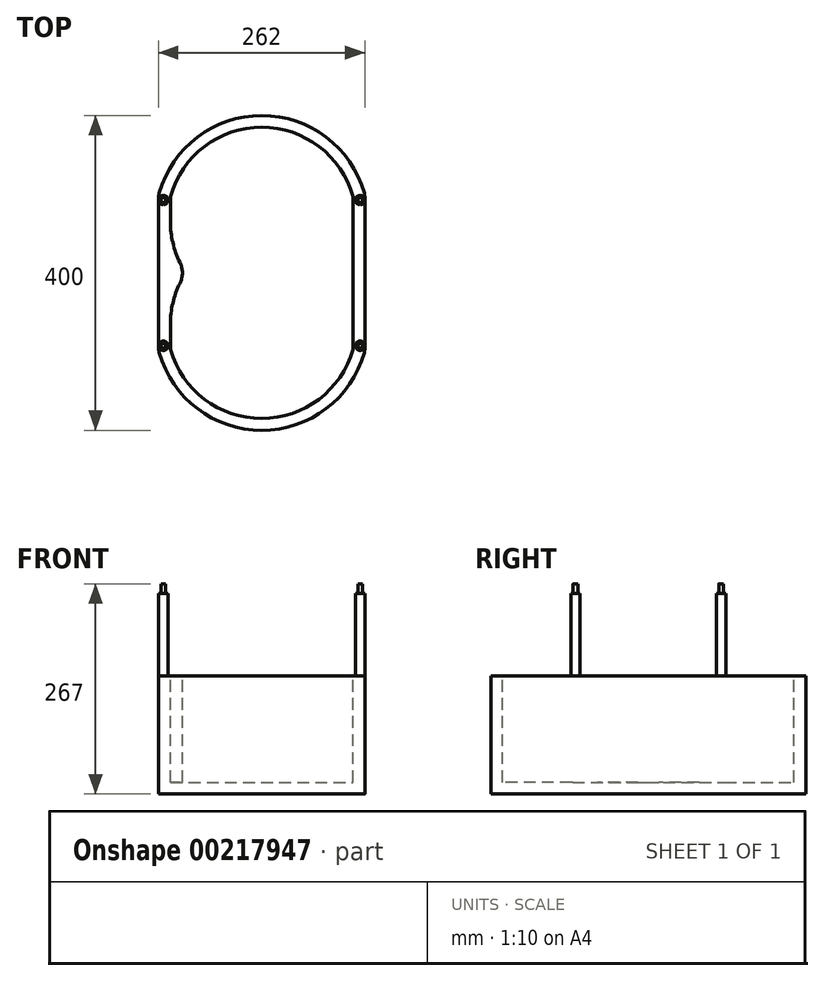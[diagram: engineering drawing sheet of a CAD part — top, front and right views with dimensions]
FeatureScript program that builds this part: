
annotation { "Feature Type Name" : "Feature", "Feature Type Description" : "" }
export const myFeature = defineFeature(function(context is Context, id is Id, definition is map)
    precondition{}
    {
        {
            var Q0;
            Q0=qCreatedBy(makeId("Top.planeOp"),FACE);
            var sketch = newSketch(context, id + "F0", { "sketchPlane" : qUnion([Q0])});
            skLineSegment(sketch, "E0.left", {"start": v(-131, -95.86) * mm, "end": v(-131, 95.86) * mm});
            skLineSegment(sketch, "E0.right", {"start": v(131, -95.86) * mm, "end": v(131, 95.86) * mm});
            skLineSegment(sketch, "E1", {"start": v(0, 64.71) * mm, "end": v(0, -64.71) * mm, "construction": true});
            skArc(sketch, "E2", {"start": v(-130.26, -101.26) * mm, "mid": v(0, -200) * mm, "end": v(130.26, -101.26) * mm});
            skArc(sketch, "E3", {"start": v(130.26, 101.26) * mm, "mid": v(0, 200) * mm, "end": v(-130.26, 101.26) * mm});
            skCircle(sketch, "E4", {"center": v(125, -92.5) * mm, "radius": 6 * mm});
            skCircle(sketch, "E5", {"center": v(-125, -92.5) * mm, "radius": 6 * mm});
            skCircle(sketch, "E6", {"center": v(-125, 92.5) * mm, "radius": 6 * mm});
            skCircle(sketch, "E7", {"center": v(125, 92.5) * mm, "radius": 6 * mm});
            skLineSegment(sketch, "E8", {"start": v(131, 0) * mm, "end": v(-131, 0) * mm, "construction": true});
            skLineSegment(sketch, "E9", {"start": v(-131, -98.5) * mm, "end": v(131, -98.5) * mm, "construction": true});
            skPoint(sketch, "E10.visualSharp", {"position": v(131, -98.5) * mm});
            skArc(sketch, "E10.filletArc", {"start": v(130.26, -101.26) * mm, "mid": v(130.81, -98.59) * mm, "end": v(131, -95.86) * mm});
            skPoint(sketch, "E11.visualSharp", {"position": v(-131, -98.5) * mm});
            skArc(sketch, "E11.filletArc", {"start": v(-131, -95.86) * mm, "mid": v(-130.81, -98.59) * mm, "end": v(-130.26, -101.26) * mm});
            skPoint(sketch, "E12.visualSharp", {"position": v(131, 98.5) * mm});
            skArc(sketch, "E12.filletArc", {"start": v(131, 95.86) * mm, "mid": v(130.81, 98.59) * mm, "end": v(130.26, 101.26) * mm});
            skPoint(sketch, "E13.visualSharp", {"position": v(-131, 98.5) * mm});
            skArc(sketch, "E13.filletArc", {"start": v(-130.26, 101.26) * mm, "mid": v(-130.81, 98.59) * mm, "end": v(-131, 95.86) * mm});
            skSolve(sketch);
        }
        {
            var Q0;
            Q0=makeQuery(id+"F0.imprint","IMPRINT",FACE,{"disambiguationData":[TD([[makeQuery(id+"F0.imprint","IMPRINT",EDGE,{"derivedFrom":sQuery(id+"F0.wireOp",EDGE,"E0.left")}),-1.0]])]});
            var Q1;
            Q1=makeQuery(id+"F0.imprint","IMPRINT",FACE,{"disambiguationData":[TD([[makeQuery(id+"F0.imprint","IMPRINT",EDGE,{"derivedFrom":sQuery(id+"F0.wireOp",EDGE,"E5")}),1.0]])]});
            var Q2;
            Q2=makeQuery(id+"F0.imprint","IMPRINT",FACE,{"disambiguationData":[TD([[makeQuery(id+"F0.imprint","IMPRINT",EDGE,{"derivedFrom":sQuery(id+"F0.wireOp",EDGE,"E6")}),1.0]])]});
            var Q3;
            Q3=makeQuery(id+"F0.imprint","IMPRINT",FACE,{"disambiguationData":[TD([[makeQuery(id+"F0.imprint","IMPRINT",EDGE,{"derivedFrom":sQuery(id+"F0.wireOp",EDGE,"E4")}),1.0]])]});
            var Q4;
            Q4=makeQuery(id+"F0.imprint","IMPRINT",FACE,{"disambiguationData":[TD([[makeQuery(id+"F0.imprint","IMPRINT",EDGE,{"derivedFrom":sQuery(id+"F0.wireOp",EDGE,"E7")}),1.0]])]});
            extrude(context, id + "F1", {"entities" : qUnion([Q0, Q1, Q2, Q3, Q4]), "oppositeDirection" : true, "depth" : 150 * mm});
        }
        {
            var Q0;
            Q0=makeQuery(id+"F1.opExtrude","CAP_FACE",FACE,{"disambiguationData":[OSD([sQuery(id+"F0.wireOp",EDGE,"E0.left"),sQuery(id+"F0.wireOp",EDGE,"E0.right"),sQuery(id+"F0.wireOp",EDGE,"E2"),sQuery(id+"F0.wireOp",EDGE,"E3")])],"isStart":true});
            shell(context, id + "F2", {"entities" : qUnion([Q0]), "thickness" : 15 * mm});
        }
        {
            var Q0;
            Q0=makeQuery(id+"F1.opExtrude","CAP_FACE",FACE,{"disambiguationData":[OSD([sQuery(id+"F0.wireOp",EDGE,"E0.left"),sQuery(id+"F0.wireOp",EDGE,"E0.right"),sQuery(id+"F0.wireOp",EDGE,"E2"),sQuery(id+"F0.wireOp",EDGE,"E3")])],"isStart":true});
            var sketch = newSketch(context, id + "F3", { "sketchPlane" : qUnion([Q0])});
            skArc(sketch, "E14.0", {"start": v(115.81, 97.2) * mm, "mid": v(0, 185) * mm, "end": v(-115.81, 97.2) * mm, "construction": true});
            skArc(sketch, "E15.0", {"start": v(-115.81, -97.2) * mm, "mid": v(0, -185) * mm, "end": v(115.81, -97.2) * mm, "construction": true});
            skLineSegment(sketch, "E16", {"start": v(115.81, 97.2) * mm, "end": v(115.81, -97.2) * mm, "construction": true});
            skArc(sketch, "E17", {"start": v(-116, 64.71) * mm, "mid": v(-112.96, 38.31) * mm, "end": v(-103.98, 13.3) * mm});
            skArc(sketch, "E18.trimOffspring", {"start": v(-103.98, -13.3) * mm, "mid": v(-112.96, -38.31) * mm, "end": v(-116, -64.71) * mm});
            skPoint(sketch, "E19.visualSharp", {"position": v(-96.27, 0) * mm});
            skArc(sketch, "E19.filletArc", {"start": v(-103.98, -13.3) * mm, "mid": v(-100.87, 0) * mm, "end": v(-103.98, 13.3) * mm});
            skLineSegment(sketch, "E20", {"start": v(-116, 64.71) * mm, "end": v(-116, -64.71) * mm});
            skLineSegment(sketch, "E21.0", {"start": v(-116, -95.86) * mm, "end": v(-116, 95.86) * mm, "construction": true});
            skSolve(sketch);
        }
        {
            var Q0;
            Q0=makeQuery(id+"F3.imprint","IMPRINT",FACE,{"disambiguationData":[TD([[makeQuery(id+"F3.imprint","IMPRINT",EDGE,{"derivedFrom":sQuery(id+"F3.wireOp",EDGE,"mgu8ekuD-Uo2P-4ZkQ-XR2Q-GfawbIWd2U9V")}),-1.0]])]});
            var Q1;
            Q1=makeQuery(id+"F3.imprint","IMPRINT",FACE,{"disambiguationData":[TD([[makeQuery(id+"F3.imprint","IMPRINT",EDGE,{"derivedFrom":sQuery(id+"F3.wireOp",EDGE,"3d6fd293-1861-4e58-a6de-7b1db9199994.trimOffspring")}),-1.0]])]});
            var Q2;
            Q2=makeQuery(id+"F3.imprint","IMPRINT",FACE,{"disambiguationData":[TD([[makeQuery(id+"F3.imprint","IMPRINT",EDGE,{"derivedFrom":sQuery(id+"F3.wireOp",EDGE,"E17")}),-1.0]])]});
            extrude(context, id + "F4", {"entities" : qUnion([Q0, Q1, Q2]), "operationType" : NewBodyOperationType.ADD, "endBound" : BoundingType.UP_TO_NEXT, "oppositeDirection" : true, "depth" : 25 * mm});
        }
        {
            var Q0;
            Q0=makeQuery(id+"F0.imprint","IMPRINT",FACE,{"disambiguationData":[TD([[makeQuery(id+"F0.imprint","IMPRINT",EDGE,{"derivedFrom":sQuery(id+"F0.wireOp",EDGE,"E4")}),1.0]])]});
            var Q1;
            Q1=makeQuery(id+"F0.imprint","IMPRINT",FACE,{"disambiguationData":[TD([[makeQuery(id+"F0.imprint","IMPRINT",EDGE,{"derivedFrom":sQuery(id+"F0.wireOp",EDGE,"E7")}),1.0]])]});
            var Q2;
            Q2=makeQuery(id+"F0.imprint","IMPRINT",FACE,{"disambiguationData":[TD([[makeQuery(id+"F0.imprint","IMPRINT",EDGE,{"derivedFrom":sQuery(id+"F0.wireOp",EDGE,"E6")}),1.0]])]});
            var Q3;
            Q3=makeQuery(id+"F0.imprint","IMPRINT",FACE,{"disambiguationData":[TD([[makeQuery(id+"F0.imprint","IMPRINT",EDGE,{"derivedFrom":sQuery(id+"F0.wireOp",EDGE,"E5")}),1.0]])]});
            extrude(context, id + "F5", {"entities" : qUnion([Q0, Q1, Q2, Q3]), "operationType" : NewBodyOperationType.ADD, "depth" : 105 * mm});
        }
        {
            var Q0;
            Q0=makeQuery(id+"F5.opExtrude","CAP_FACE",FACE,{"disambiguationData":[OSD([sQuery(id+"F0.wireOp",EDGE,"E4")])],"isStart":false});
            var sketch = newSketch(context, id + "F6", { "sketchPlane" : qUnion([Q0])});
            skCircle(sketch, "E22", {"center": v(-125, -92.5) * mm, "radius": 3 * mm});
            skCircle(sketch, "E23", {"center": v(125, -92.5) * mm, "radius": 3 * mm});
            skCircle(sketch, "E24", {"center": v(125, 92.5) * mm, "radius": 3 * mm});
            skCircle(sketch, "E25", {"center": v(-125, 92.5) * mm, "radius": 3 * mm});
            skCircle(sketch, "E26.0", {"center": v(125, 92.5) * mm, "radius": 6 * mm, "construction": true});
            skCircle(sketch, "E27.0", {"center": v(125, -92.5) * mm, "radius": 6 * mm, "construction": true});
            skCircle(sketch, "E28.0", {"center": v(-125, -92.5) * mm, "radius": 6 * mm, "construction": true});
            skCircle(sketch, "E29.0", {"center": v(-125, 92.5) * mm, "radius": 6 * mm, "construction": true});
            skSolve(sketch);
        }
        {
            var Q0;
            Q0=makeQuery(id+"F6.imprint","IMPRINT",FACE,{"disambiguationData":[TD([[makeQuery(id+"F6.imprint","IMPRINT",EDGE,{"derivedFrom":sQuery(id+"F6.wireOp",EDGE,"E23")}),1.0]])]});
            var Q1;
            Q1=makeQuery(id+"F6.imprint","IMPRINT",FACE,{"disambiguationData":[TD([[makeQuery(id+"F6.imprint","IMPRINT",EDGE,{"derivedFrom":sQuery(id+"F6.wireOp",EDGE,"E22")}),1.0]])]});
            var Q2;
            Q2=makeQuery(id+"F6.imprint","IMPRINT",FACE,{"disambiguationData":[TD([[makeQuery(id+"F6.imprint","IMPRINT",EDGE,{"derivedFrom":sQuery(id+"F6.wireOp",EDGE,"E24")}),1.0]])]});
            var Q3;
            Q3=makeQuery(id+"F6.imprint","IMPRINT",FACE,{"disambiguationData":[TD([[makeQuery(id+"F6.imprint","IMPRINT",EDGE,{"derivedFrom":sQuery(id+"F6.wireOp",EDGE,"E25")}),1.0]])]});
            extrude(context, id + "F7", {"entities" : qUnion([Q0, Q1, Q2, Q3]), "operationType" : NewBodyOperationType.ADD, "depth" : 12 * mm});
        }
    });
